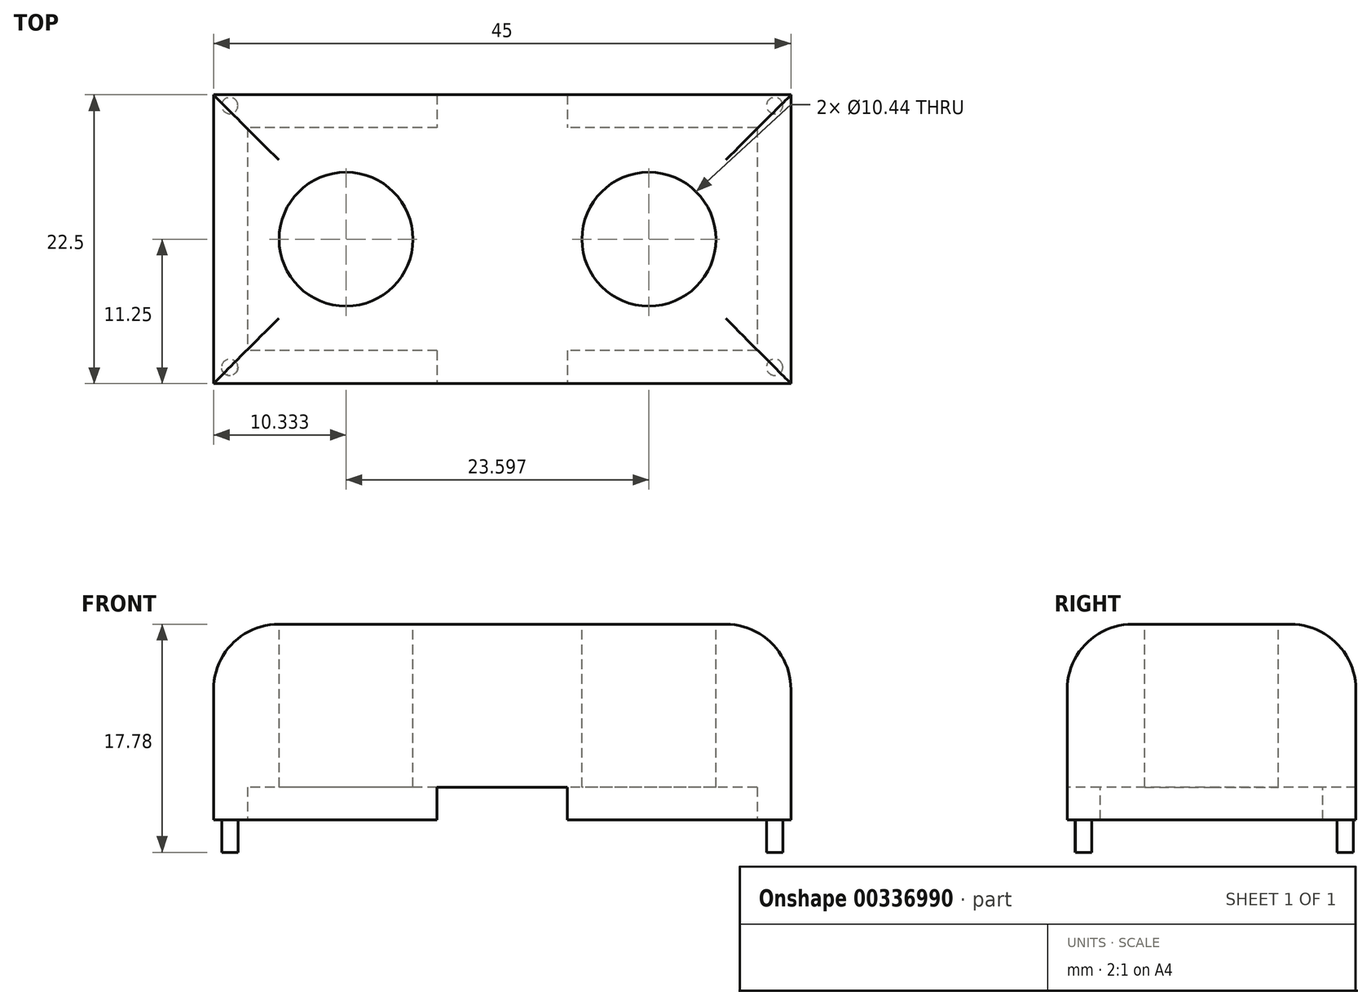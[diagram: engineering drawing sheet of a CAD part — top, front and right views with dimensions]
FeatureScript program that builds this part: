
annotation { "Feature Type Name" : "Feature", "Feature Type Description" : "" }
export const myFeature = defineFeature(function(context is Context, id is Id, definition is map)
    precondition{}
    {
        {
            var Q0;
            Q0=qCreatedBy(makeId("Top.planeOp"),FACE);
            var sketch = newSketch(context, id + "F0", { "sketchPlane" : qUnion([Q0])});
            skLineSegment(sketch, "E0.bottom", {"start": v(22.5, 11.25) * mm, "end": v(-22.5, 11.25) * mm});
            skLineSegment(sketch, "E0.top", {"start": v(22.5, -11.25) * mm, "end": v(-22.5, -11.25) * mm});
            skLineSegment(sketch, "E0.left", {"start": v(22.5, 11.25) * mm, "end": v(22.5, -11.25) * mm});
            skLineSegment(sketch, "E0.right", {"start": v(-22.5, 11.25) * mm, "end": v(-22.5, -11.25) * mm});
            skPoint(sketch, "E0.middle", {"position": v(0, 0) * mm});
            skSolve(sketch);
        }
        {
            var Q0;
            Q0 = qSketchRegion(id + "F0", true);
            extrude(context, id + "F1", {"entities" : qUnion([Q0]), "depth" : 15.24 * mm});
        }
        {
            var Q0;
            Q0=makeQuery(id+"F1.opExtrude","CAP_FACE",FACE,{"disambiguationData":[OSD([sQuery(id+"F0.wireOp",EDGE,"E0.bottom"),sQuery(id+"F0.wireOp",EDGE,"E0.top"),sQuery(id+"F0.wireOp",EDGE,"E0.left"),sQuery(id+"F0.wireOp",EDGE,"E0.right")])],"isStart":false});
            var sketch = newSketch(context, id + "F2", { "sketchPlane" : qUnion([Q0])});
            skCircle(sketch, "E1", {"center": v(-12.17, 0) * mm, "radius": 5.22 * mm});
            skCircle(sketch, "E2", {"center": v(11.43, 0) * mm, "radius": 5.22 * mm});
            skSolve(sketch);
        }
        {
            var Q0;
            Q0 = qSketchRegion(id + "F2", true);
            extrude(context, id + "F3", {"entities" : qUnion([Q0]), "operationType" : NewBodyOperationType.REMOVE, "endBound" : BoundingType.THROUGH_ALL, "oppositeDirection" : true, "depth" : 25.4 * mm});
        }
        {
            var Q0;
            Q0=makeQuery(id+"F0.imprint","IMPRINT",FACE,{"disambiguationData":[TD([[makeQuery(id+"F0.imprint","IMPRINT",EDGE,{"derivedFrom":sQuery(id+"F0.wireOp",EDGE,"E0.bottom")}),1.0]])]});
            var sketch = newSketch(context, id + "F4", { "sketchPlane" : qUnion([Q0])});
            skPoint(sketch, "E3.middle", {"position": v(0, 0) * mm});
            skCircle(sketch, "E4", {"center": v(-21.23, -9.99) * mm, "radius": 0.64 * mm});
            skCircle(sketch, "E5", {"center": v(21.23, -9.98) * mm, "radius": 0.64 * mm});
            skCircle(sketch, "E6", {"center": v(21.23, 10.42) * mm, "radius": 0.64 * mm});
            skCircle(sketch, "E7", {"center": v(-21.23, 10.42) * mm, "radius": 0.64 * mm});
            skPoint(sketch, "E3.left.start.orphan", {"position": v(-19.96, -8.7) * mm});
            skPoint(sketch, "E3.top.start.orphan", {"position": v(-19.96, 8.7) * mm});
            skPoint(sketch, "E3.right.end.orphan", {"position": v(19.96, 8.7) * mm});
            skPoint(sketch, "E3.right.start.orphan", {"position": v(19.96, -8.7) * mm});
            skSolve(sketch);
        }
        {
            var Q0;
            Q0 = qSketchRegion(id + "F4", true);
            extrude(context, id + "F5", {"entities" : qUnion([Q0]), "depth" : -2.54 * mm});
        }
        {
            var Q0;
            Q0=makeQuery(id+"F5.opExtrude","CAP_FACE",FACE,{"disambiguationData":[OSD([sQuery(id+"F4.wireOp",EDGE,"E4"),sQuery(id+"F4.wireOp",EDGE,"E5"),sQuery(id+"F4.wireOp",EDGE,"E6"),sQuery(id+"F4.wireOp",EDGE,"E7"),sQuery(id+"F4.wireOp",EDGE,"b4O081GP-RIa0-ohmu-tcYU-JH3XeOnzlBR6"),sQuery(id+"F4.wireOp",EDGE,"iJNTEDua-cZCK-36sH-BaMI-u3GDocb22RIU"),sQuery(id+"F4.wireOp",EDGE,"liQB3p1X-CMLk-Pjzu-2UsC-YHu2LbuQZlpa"),sQuery(id+"F4.wireOp",EDGE,"7MqfjxEw-HzZ1-rnMm-tX5i-Kihl1VsWI0d4")])],"isStart":false});
            var sketch = newSketch(context, id + "F6", { "sketchPlane" : qUnion([Q0])});
            skCircle(sketch, "E8", {"center": v(-21.23, 9.98) * mm, "radius": 0.64 * mm});
            skCircle(sketch, "E9", {"center": v(21.23, 9.98) * mm, "radius": 0.64 * mm});
            skCircle(sketch, "E10", {"center": v(21.23, -9.98) * mm, "radius": 0.64 * mm});
            skCircle(sketch, "E11", {"center": v(-21.23, -9.98) * mm, "radius": 0.64 * mm});
            skSolve(sketch);
        }
        {
            var Q0;
            Q0=makeQuery(id+"F6.imprint","IMPRINT",FACE,{"disambiguationData":[TD([[makeQuery(id+"F6.imprint","IMPRINT",EDGE,{"disambiguationData":[OD(1.0)],"derivedFrom":sQuery(id+"F6.wireOp",EDGE,"E8")}),-1.0]])]});
            var Q1;
            Q1 = qSketchRegion(id + "F4", true);
            extrude(context, id + "F7", {"entities" : qUnion([Q0, Q1]), "operationType" : NewBodyOperationType.ADD, "oppositeDirection" : true, "depth" : 2.54 * mm});
        }
        {
            var Q0;
            Q0=makeQuery(id+"F0.imprint","IMPRINT",FACE,{"disambiguationData":[TD([[makeQuery(id+"F0.imprint","IMPRINT",EDGE,{"derivedFrom":sQuery(id+"F0.wireOp",EDGE,"E0.bottom")}),1.0]])]});
            var sketch = newSketch(context, id + "F8", { "sketchPlane" : qUnion([Q0])});
            skLineSegment(sketch, "E12.bottom", {"start": v(19.86, 8.68) * mm, "end": v(-19.86, 8.68) * mm});
            skLineSegment(sketch, "E12.top", {"start": v(19.86, -8.68) * mm, "end": v(-19.86, -8.68) * mm});
            skLineSegment(sketch, "E12.left", {"start": v(19.86, 8.68) * mm, "end": v(19.86, -8.68) * mm});
            skLineSegment(sketch, "E12.right", {"start": v(-19.86, 8.68) * mm, "end": v(-19.86, -8.68) * mm});
            skPoint(sketch, "E12.middle", {"position": v(0, 0) * mm});
            skSolve(sketch);
        }
        {
            var Q0;
            Q0=makeQuery(id+"F8.imprint","IMPRINT",FACE,{"disambiguationData":[TD([[makeQuery(id+"F8.imprint","IMPRINT",EDGE,{"derivedFrom":sQuery(id+"F8.wireOp",EDGE,"E12.bottom")}),1.0]])]});
            extrude(context, id + "F9", {"entities" : qUnion([Q0]), "operationType" : NewBodyOperationType.REMOVE, "oppositeDirection" : true, "depth" : -2.54 * mm});
        }
        {
            var Q0;
            Q0=makeQuery(id+"F1.opExtrude","CAP_FACE",FACE,{"disambiguationData":[OSD([sQuery(id+"F0.wireOp",EDGE,"E0.bottom"),sQuery(id+"F0.wireOp",EDGE,"E0.top"),sQuery(id+"F0.wireOp",EDGE,"E0.left"),sQuery(id+"F0.wireOp",EDGE,"E0.right")])],"isStart":false});
            var sketch = newSketch(context, id + "F10", { "sketchPlane" : qUnion([Q0])});
            skCircle(sketch, "E13", {"center": v(11.43, 0) * mm, "radius": 5.23 * mm});
            skCircle(sketch, "E14", {"center": v(-12.17, 0) * mm, "radius": 5.23 * mm});
            skLineSegment(sketch, "E15.bottom", {"start": v(-22.5, -11.25) * mm, "end": v(22.5, -11.25) * mm});
            skLineSegment(sketch, "E15.top", {"start": v(-22.5, 11.25) * mm, "end": v(22.5, 11.25) * mm});
            skLineSegment(sketch, "E15.left", {"start": v(-22.5, -11.25) * mm, "end": v(-22.5, 11.25) * mm});
            skLineSegment(sketch, "E15.right", {"start": v(22.5, -11.25) * mm, "end": v(22.5, 11.25) * mm});
            skSolve(sketch);
        }
        {
            var Q0;
            Q0=makeQuery(id+"F1.opExtrude","SWEPT_FACE",FACE,{"disambiguationData":[OSD([sQuery(id+"F0.wireOp",EDGE,"E0.top")])]});
            var sketch = newSketch(context, id + "F11", { "sketchPlane" : qUnion([Q0])});
            skLineSegment(sketch, "E16.bottom", {"start": v(-5.08, 0) * mm, "end": v(5.08, 0) * mm});
            skLineSegment(sketch, "E16.top", {"start": v(-5.08, 2.54) * mm, "end": v(5.08, 2.54) * mm});
            skLineSegment(sketch, "E16.left", {"start": v(-5.08, 0) * mm, "end": v(-5.08, 2.54) * mm});
            skLineSegment(sketch, "E16.right", {"start": v(5.08, 0) * mm, "end": v(5.08, 2.54) * mm});
            skSolve(sketch);
        }
        {
            var Q0;
            Q0=makeQuery(id+"F11.imprint","IMPRINT",FACE,{"disambiguationData":[TD([[makeQuery(id+"F11.imprint","IMPRINT",EDGE,{"derivedFrom":sQuery(id+"F11.wireOp",EDGE,"E16.bottom")}),-1.0]])]});
            extrude(context, id + "F12", {"entities" : qUnion([Q0]), "operationType" : NewBodyOperationType.REMOVE, "endBound" : BoundingType.THROUGH_ALL, "oppositeDirection" : true, "depth" : 25.4 * mm});
        }
        {
            var Q0;
            Q0 = qSketchRegion(id + "F10", true);
            extrude(context, id + "F13", {"entities" : qUnion([Q0]), "operationType" : NewBodyOperationType.ADD, "depth" : -10.16 * mm});
        }
        {
            var Q0;
            Q0=makeQuery(id+"F1.opExtrude","CAP_EDGE",EDGE,{"disambiguationData":[OSD([sQuery(id+"F0.wireOp",EDGE,"E0.right")])],"isStart":false});
            var Q1;
            Q1=makeQuery(id+"F1.opExtrude","CAP_EDGE",EDGE,{"disambiguationData":[OSD([sQuery(id+"F0.wireOp",EDGE,"E0.bottom")])],"isStart":false});
            var Q2;
            Q2=makeQuery(id+"F1.opExtrude","CAP_EDGE",EDGE,{"disambiguationData":[OSD([sQuery(id+"F0.wireOp",EDGE,"E0.top")])],"isStart":false});
            var Q3;
            Q3=makeQuery(id+"F1.opExtrude","CAP_EDGE",EDGE,{"disambiguationData":[OSD([sQuery(id+"F0.wireOp",EDGE,"E0.left")])],"isStart":false});
            fillet(context, id + "F14", {"entities" : qUnion([Q0, Q1, Q2, Q3]), "radius" : 5.08 * mm, "tangentPropagation" : true, "allowEdgeOverflow" : false});
        }
    });
